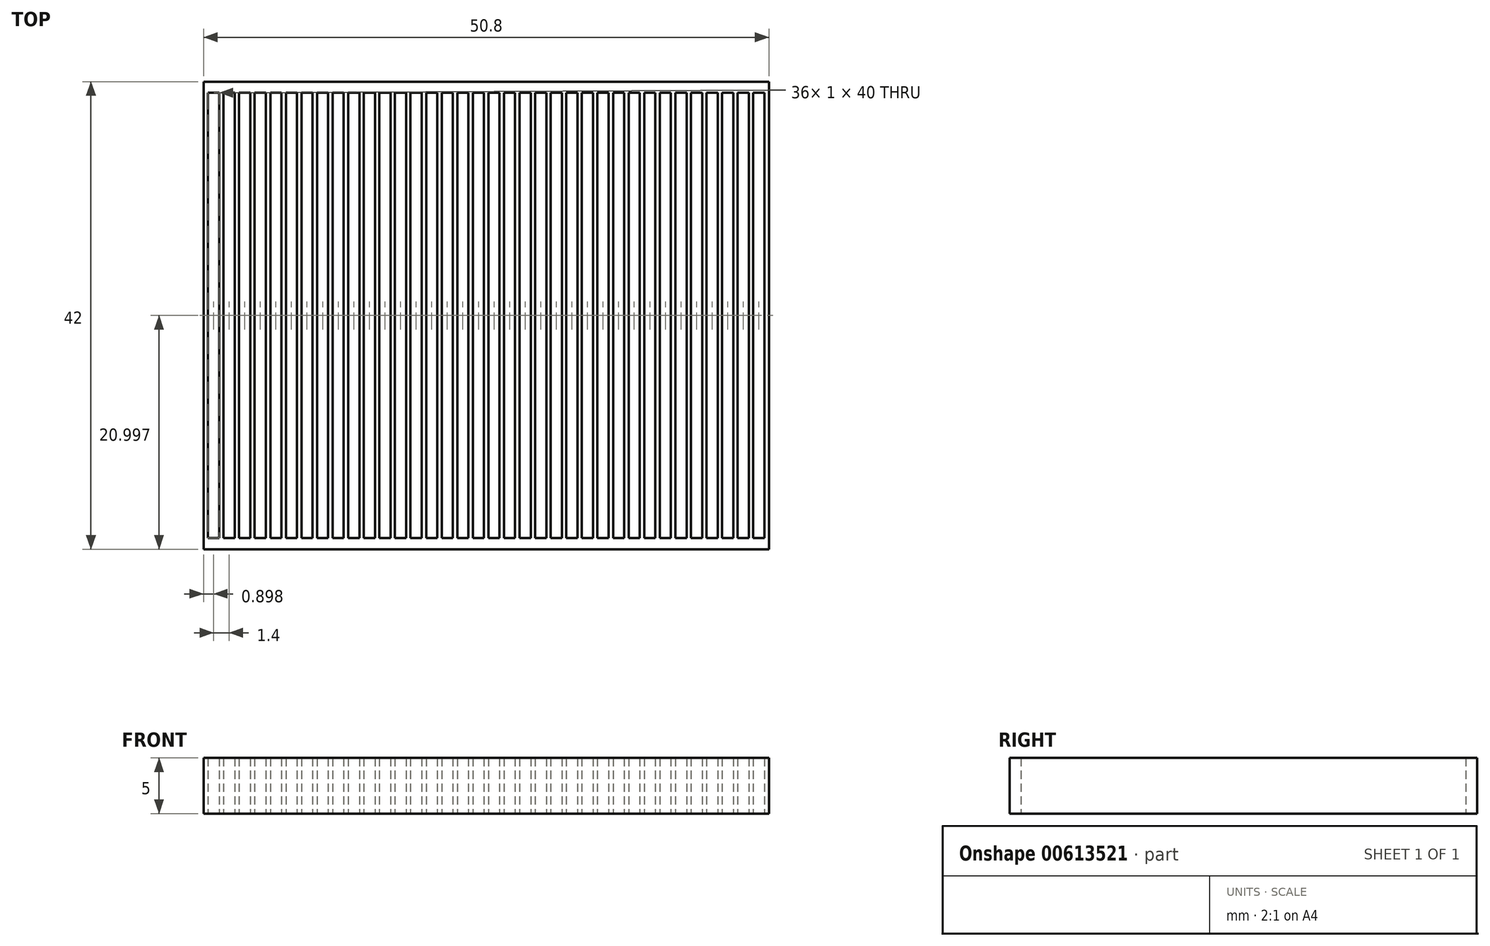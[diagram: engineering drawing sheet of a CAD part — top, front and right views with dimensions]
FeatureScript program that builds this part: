
annotation { "Feature Type Name" : "Feature", "Feature Type Description" : "" }
export const myFeature = defineFeature(function(context is Context, id is Id, definition is map)
    precondition{}
    {
        {
            var Q0;
            Q0=qCreatedBy(makeId("Top.planeOp"),FACE);
            var sketch = newSketch(context, id + "F0", { "sketchPlane" : qUnion([Q0])});
            skLineSegment(sketch, "E0", {"start": v(-21.82, 27.89) * mm, "end": v(-21.82, -14.11) * mm});
            skLineSegment(sketch, "E1", {"start": v(-21.82, -14.11) * mm, "end": v(-21.42, -14.11) * mm});
            skLineSegment(sketch, "E2", {"start": v(-21.42, -14.11) * mm, "end": v(-21.42, 26.89) * mm});
            skLineSegment(sketch, "E3", {"start": v(-21.42, 26.89) * mm, "end": v(-20.42, 26.89) * mm});
            skLineSegment(sketch, "E4", {"start": v(-20.42, 26.89) * mm, "end": v(-20.42, -14.11) * mm});
            skLineSegment(sketch, "E5", {"start": v(-20.42, -14.11) * mm, "end": v(-20.02, -14.11) * mm});
            skLineSegment(sketch, "E6", {"start": v(-20.02, -14.11) * mm, "end": v(-20.02, 26.89) * mm});
            skLineSegment(sketch, "E7", {"start": v(-20.02, 26.89) * mm, "end": v(-19.02, 26.89) * mm});
            skLineSegment(sketch, "E8", {"start": v(-19.02, 26.89) * mm, "end": v(-19.02, -14.11) * mm});
            skLineSegment(sketch, "E9", {"start": v(-19.02, -14.11) * mm, "end": v(-18.62, -14.11) * mm});
            skLineSegment(sketch, "E10", {"start": v(-18.62, -14.11) * mm, "end": v(-18.62, 26.89) * mm});
            skLineSegment(sketch, "E11", {"start": v(-18.62, 26.89) * mm, "end": v(-17.62, 26.89) * mm});
            skLineSegment(sketch, "E12", {"start": v(-17.62, 26.89) * mm, "end": v(-17.62, -14.11) * mm});
            skLineSegment(sketch, "E13", {"start": v(-17.62, -14.11) * mm, "end": v(-17.22, -14.11) * mm});
            skLineSegment(sketch, "E14", {"start": v(-17.22, -14.11) * mm, "end": v(-17.22, 26.89) * mm});
            skLineSegment(sketch, "E15", {"start": v(-17.22, 26.89) * mm, "end": v(-16.22, 26.89) * mm});
            skLineSegment(sketch, "E16", {"start": v(-16.22, 26.89) * mm, "end": v(-16.22, -14.11) * mm});
            skLineSegment(sketch, "E17", {"start": v(-16.22, -14.11) * mm, "end": v(-15.82, -14.11) * mm});
            skLineSegment(sketch, "E18", {"start": v(-15.82, -14.11) * mm, "end": v(-15.82, 26.89) * mm});
            skLineSegment(sketch, "E19", {"start": v(-15.82, 26.89) * mm, "end": v(-14.82, 26.89) * mm});
            skLineSegment(sketch, "E20", {"start": v(-14.82, 26.89) * mm, "end": v(-14.82, -14.11) * mm});
            skLineSegment(sketch, "E21", {"start": v(-14.82, -14.11) * mm, "end": v(-14.42, -14.11) * mm});
            skLineSegment(sketch, "E22", {"start": v(-14.42, -14.11) * mm, "end": v(-14.42, 26.89) * mm});
            skLineSegment(sketch, "E23", {"start": v(-14.42, 26.89) * mm, "end": v(-13.42, 26.89) * mm});
            skLineSegment(sketch, "E24", {"start": v(-13.42, 26.89) * mm, "end": v(-13.42, -14.11) * mm});
            skLineSegment(sketch, "E25", {"start": v(-13.42, -14.11) * mm, "end": v(-13.02, -14.11) * mm});
            skLineSegment(sketch, "E26", {"start": v(-13.02, -14.11) * mm, "end": v(-13.02, 26.89) * mm});
            skLineSegment(sketch, "E27", {"start": v(-13.02, 26.89) * mm, "end": v(-12.02, 26.89) * mm});
            skLineSegment(sketch, "E28", {"start": v(-12.02, 26.89) * mm, "end": v(-12.02, -14.11) * mm});
            skLineSegment(sketch, "E29", {"start": v(-12.02, -14.11) * mm, "end": v(-11.62, -14.11) * mm});
            skLineSegment(sketch, "E30", {"start": v(-11.62, -14.11) * mm, "end": v(-11.62, 26.89) * mm});
            skLineSegment(sketch, "E31", {"start": v(-11.62, 26.89) * mm, "end": v(-10.62, 26.89) * mm});
            skLineSegment(sketch, "E32", {"start": v(-10.62, 26.89) * mm, "end": v(-10.62, -14.11) * mm});
            skLineSegment(sketch, "E33", {"start": v(-10.62, -14.11) * mm, "end": v(-10.22, -14.11) * mm});
            skLineSegment(sketch, "E34", {"start": v(-10.22, -14.11) * mm, "end": v(-10.22, 26.89) * mm});
            skLineSegment(sketch, "E35", {"start": v(-10.22, 26.89) * mm, "end": v(-9.22, 26.89) * mm});
            skLineSegment(sketch, "E36", {"start": v(-9.22, 26.89) * mm, "end": v(-9.22, -14.11) * mm});
            skLineSegment(sketch, "E37", {"start": v(-9.22, -14.11) * mm, "end": v(-8.82, -14.11) * mm});
            skLineSegment(sketch, "E38", {"start": v(-8.82, -14.11) * mm, "end": v(-8.82, 26.89) * mm});
            skLineSegment(sketch, "E39", {"start": v(-8.82, 26.89) * mm, "end": v(-7.82, 26.89) * mm});
            skLineSegment(sketch, "E40", {"start": v(-7.82, 26.89) * mm, "end": v(-7.82, -14.11) * mm});
            skLineSegment(sketch, "E41", {"start": v(-7.82, -14.11) * mm, "end": v(-7.42, -14.11) * mm});
            skLineSegment(sketch, "E42", {"start": v(-7.42, -14.11) * mm, "end": v(-7.42, 26.89) * mm});
            skLineSegment(sketch, "E43", {"start": v(-7.42, 26.89) * mm, "end": v(-6.42, 26.89) * mm});
            skLineSegment(sketch, "E44", {"start": v(-6.42, 26.89) * mm, "end": v(-6.42, -14.11) * mm});
            skLineSegment(sketch, "E45", {"start": v(-6.42, -14.11) * mm, "end": v(-6.02, -14.11) * mm});
            skLineSegment(sketch, "E46", {"start": v(-6.02, -14.11) * mm, "end": v(-6.02, 26.89) * mm});
            skLineSegment(sketch, "E47", {"start": v(-6.02, 26.89) * mm, "end": v(-5.02, 26.89) * mm});
            skLineSegment(sketch, "E48", {"start": v(-5.02, 26.89) * mm, "end": v(-5.02, -14.11) * mm});
            skLineSegment(sketch, "E49", {"start": v(-5.02, -14.11) * mm, "end": v(-4.62, -14.11) * mm});
            skLineSegment(sketch, "E50", {"start": v(-4.62, -14.11) * mm, "end": v(-4.62, 26.89) * mm});
            skLineSegment(sketch, "E51", {"start": v(-4.62, 26.89) * mm, "end": v(-3.62, 26.89) * mm});
            skLineSegment(sketch, "E52", {"start": v(-3.62, 26.89) * mm, "end": v(-3.62, -14.11) * mm});
            skLineSegment(sketch, "E53", {"start": v(-3.62, -14.11) * mm, "end": v(-3.22, -14.11) * mm});
            skLineSegment(sketch, "E54", {"start": v(-3.22, -14.11) * mm, "end": v(-3.22, 26.89) * mm});
            skLineSegment(sketch, "E55", {"start": v(-3.22, 26.89) * mm, "end": v(-2.22, 26.89) * mm});
            skLineSegment(sketch, "E56", {"start": v(-2.22, 26.89) * mm, "end": v(-2.22, -14.11) * mm});
            skLineSegment(sketch, "E57", {"start": v(-2.22, -14.11) * mm, "end": v(-1.82, -14.11) * mm});
            skLineSegment(sketch, "E58", {"start": v(-1.82, -14.11) * mm, "end": v(-1.82, 26.89) * mm});
            skLineSegment(sketch, "E59", {"start": v(-1.82, 26.89) * mm, "end": v(-0.82, 26.89) * mm});
            skLineSegment(sketch, "E60", {"start": v(-0.82, 26.89) * mm, "end": v(-0.82, -14.11) * mm});
            skLineSegment(sketch, "E61", {"start": v(-0.82, -14.11) * mm, "end": v(-0.42, -14.11) * mm});
            skLineSegment(sketch, "E62", {"start": v(-0.42, -14.11) * mm, "end": v(-0.42, 26.89) * mm});
            skLineSegment(sketch, "E63", {"start": v(-0.42, 26.89) * mm, "end": v(0.58, 26.89) * mm});
            skLineSegment(sketch, "E64", {"start": v(0.58, 26.89) * mm, "end": v(0.58, -14.11) * mm});
            skLineSegment(sketch, "E65", {"start": v(0.58, -14.11) * mm, "end": v(0.98, -14.11) * mm});
            skLineSegment(sketch, "E66", {"start": v(0.98, -14.11) * mm, "end": v(0.98, 26.89) * mm});
            skLineSegment(sketch, "E67", {"start": v(0.98, 26.89) * mm, "end": v(1.98, 26.89) * mm});
            skLineSegment(sketch, "E68", {"start": v(1.98, 26.89) * mm, "end": v(1.98, -14.11) * mm});
            skLineSegment(sketch, "E69", {"start": v(1.98, -14.11) * mm, "end": v(2.38, -14.11) * mm});
            skLineSegment(sketch, "E70", {"start": v(2.38, -14.11) * mm, "end": v(2.38, 26.89) * mm});
            skLineSegment(sketch, "E71", {"start": v(2.38, 26.89) * mm, "end": v(3.38, 26.89) * mm});
            skLineSegment(sketch, "E72", {"start": v(3.38, 26.89) * mm, "end": v(3.38, -14.11) * mm});
            skLineSegment(sketch, "E73", {"start": v(3.38, -14.11) * mm, "end": v(3.78, -14.11) * mm});
            skLineSegment(sketch, "E74", {"start": v(3.78, -14.11) * mm, "end": v(3.78, 26.89) * mm});
            skLineSegment(sketch, "E75", {"start": v(3.78, 26.89) * mm, "end": v(4.78, 26.89) * mm});
            skLineSegment(sketch, "E76", {"start": v(4.78, 26.89) * mm, "end": v(4.78, -14.11) * mm});
            skLineSegment(sketch, "E77", {"start": v(4.78, -14.11) * mm, "end": v(5.18, -14.11) * mm});
            skLineSegment(sketch, "E78", {"start": v(5.18, -14.11) * mm, "end": v(5.18, 26.89) * mm});
            skLineSegment(sketch, "E79", {"start": v(5.18, 26.89) * mm, "end": v(6.18, 26.89) * mm});
            skLineSegment(sketch, "E80", {"start": v(6.18, 26.89) * mm, "end": v(6.18, -14.11) * mm});
            skLineSegment(sketch, "E81", {"start": v(6.18, -14.11) * mm, "end": v(6.58, -14.11) * mm});
            skLineSegment(sketch, "E82", {"start": v(6.58, -14.11) * mm, "end": v(6.58, 26.89) * mm});
            skLineSegment(sketch, "E83", {"start": v(6.58, 26.89) * mm, "end": v(7.58, 26.89) * mm});
            skLineSegment(sketch, "E84", {"start": v(7.58, 26.89) * mm, "end": v(7.58, -14.11) * mm});
            skLineSegment(sketch, "E85", {"start": v(7.58, -14.11) * mm, "end": v(7.98, -14.11) * mm});
            skLineSegment(sketch, "E86", {"start": v(7.98, -14.11) * mm, "end": v(7.98, 26.89) * mm});
            skLineSegment(sketch, "E87", {"start": v(7.98, 26.89) * mm, "end": v(8.98, 26.89) * mm});
            skLineSegment(sketch, "E88", {"start": v(8.98, 26.89) * mm, "end": v(8.98, -14.11) * mm});
            skLineSegment(sketch, "E89", {"start": v(8.98, -14.11) * mm, "end": v(9.38, -14.11) * mm});
            skLineSegment(sketch, "E90", {"start": v(9.38, -14.11) * mm, "end": v(9.38, 26.89) * mm});
            skLineSegment(sketch, "E91", {"start": v(9.38, 26.89) * mm, "end": v(10.38, 26.89) * mm});
            skLineSegment(sketch, "E92", {"start": v(10.38, 26.89) * mm, "end": v(10.38, -14.11) * mm});
            skLineSegment(sketch, "E93", {"start": v(10.38, -14.11) * mm, "end": v(10.78, -14.11) * mm});
            skLineSegment(sketch, "E94", {"start": v(10.78, -14.11) * mm, "end": v(10.78, 26.89) * mm});
            skLineSegment(sketch, "E95", {"start": v(10.78, 26.89) * mm, "end": v(11.78, 26.89) * mm});
            skLineSegment(sketch, "E96", {"start": v(11.78, 26.89) * mm, "end": v(11.78, -14.11) * mm});
            skLineSegment(sketch, "E97", {"start": v(11.78, -14.11) * mm, "end": v(12.18, -14.11) * mm});
            skLineSegment(sketch, "E98", {"start": v(12.18, -14.11) * mm, "end": v(12.18, 26.89) * mm});
            skLineSegment(sketch, "E99", {"start": v(12.18, 26.89) * mm, "end": v(13.18, 26.89) * mm});
            skLineSegment(sketch, "E100", {"start": v(13.18, 26.89) * mm, "end": v(13.18, -14.11) * mm});
            skLineSegment(sketch, "E101", {"start": v(13.18, -14.11) * mm, "end": v(13.58, -14.11) * mm});
            skLineSegment(sketch, "E102", {"start": v(13.58, -14.11) * mm, "end": v(13.58, 26.89) * mm});
            skLineSegment(sketch, "E103", {"start": v(13.58, 26.89) * mm, "end": v(14.58, 26.89) * mm});
            skLineSegment(sketch, "E104", {"start": v(14.58, 26.89) * mm, "end": v(14.58, -14.11) * mm});
            skLineSegment(sketch, "E105", {"start": v(14.58, -14.11) * mm, "end": v(14.98, -14.11) * mm});
            skLineSegment(sketch, "E106", {"start": v(14.98, -14.11) * mm, "end": v(14.98, 26.89) * mm});
            skLineSegment(sketch, "E107", {"start": v(14.98, 26.89) * mm, "end": v(15.98, 26.89) * mm});
            skLineSegment(sketch, "E108", {"start": v(15.98, 26.89) * mm, "end": v(15.98, -14.11) * mm});
            skLineSegment(sketch, "E109", {"start": v(15.98, -14.11) * mm, "end": v(16.38, -14.11) * mm});
            skLineSegment(sketch, "E110", {"start": v(16.38, -14.11) * mm, "end": v(16.38, 26.89) * mm});
            skLineSegment(sketch, "E111", {"start": v(16.38, 26.89) * mm, "end": v(17.38, 26.89) * mm});
            skLineSegment(sketch, "E112", {"start": v(17.38, 26.89) * mm, "end": v(17.38, -14.11) * mm});
            skLineSegment(sketch, "E113", {"start": v(17.38, -14.11) * mm, "end": v(17.78, -14.11) * mm});
            skLineSegment(sketch, "E114", {"start": v(17.78, -14.11) * mm, "end": v(17.78, 26.89) * mm});
            skLineSegment(sketch, "E115", {"start": v(17.78, 26.89) * mm, "end": v(18.78, 26.89) * mm});
            skLineSegment(sketch, "E116", {"start": v(18.78, 26.89) * mm, "end": v(18.78, -14.11) * mm});
            skLineSegment(sketch, "E117", {"start": v(18.78, -14.11) * mm, "end": v(19.18, -14.11) * mm});
            skLineSegment(sketch, "E118", {"start": v(19.18, -14.11) * mm, "end": v(19.18, 26.89) * mm});
            skLineSegment(sketch, "E119", {"start": v(19.18, 26.89) * mm, "end": v(20.18, 26.89) * mm});
            skLineSegment(sketch, "E120", {"start": v(20.18, 26.89) * mm, "end": v(20.18, -14.11) * mm});
            skLineSegment(sketch, "E121", {"start": v(20.18, -14.11) * mm, "end": v(20.58, -14.11) * mm});
            skLineSegment(sketch, "E122", {"start": v(20.58, -14.11) * mm, "end": v(20.58, 26.89) * mm});
            skLineSegment(sketch, "E123", {"start": v(20.58, 26.89) * mm, "end": v(21.58, 26.89) * mm});
            skLineSegment(sketch, "E124", {"start": v(21.58, 26.89) * mm, "end": v(21.58, -14.11) * mm});
            skLineSegment(sketch, "E125", {"start": v(21.58, -14.11) * mm, "end": v(21.98, -14.11) * mm});
            skLineSegment(sketch, "E126", {"start": v(21.98, -14.11) * mm, "end": v(21.98, 26.89) * mm});
            skLineSegment(sketch, "E127", {"start": v(21.98, 26.89) * mm, "end": v(22.98, 26.89) * mm});
            skLineSegment(sketch, "E128", {"start": v(22.98, 26.89) * mm, "end": v(22.98, -14.11) * mm});
            skLineSegment(sketch, "E129", {"start": v(22.98, -14.11) * mm, "end": v(23.38, -14.11) * mm});
            skLineSegment(sketch, "E130", {"start": v(23.38, -14.11) * mm, "end": v(23.38, 26.89) * mm});
            skLineSegment(sketch, "E131", {"start": v(23.38, 26.89) * mm, "end": v(24.38, 26.89) * mm});
            skLineSegment(sketch, "E132", {"start": v(24.38, 26.89) * mm, "end": v(24.38, -14.11) * mm});
            skLineSegment(sketch, "E133", {"start": v(24.38, -14.11) * mm, "end": v(24.78, -14.11) * mm});
            skLineSegment(sketch, "E134", {"start": v(24.78, -14.11) * mm, "end": v(24.78, 26.89) * mm});
            skLineSegment(sketch, "E135", {"start": v(24.78, 26.89) * mm, "end": v(25.78, 26.89) * mm});
            skLineSegment(sketch, "E136", {"start": v(25.78, 26.89) * mm, "end": v(25.78, -14.11) * mm});
            skLineSegment(sketch, "E137", {"start": v(25.78, -14.11) * mm, "end": v(26.18, -14.11) * mm});
            skLineSegment(sketch, "E138", {"start": v(26.18, -14.11) * mm, "end": v(26.18, 26.89) * mm});
            skLineSegment(sketch, "E139", {"start": v(26.18, 26.89) * mm, "end": v(27.18, 26.89) * mm});
            skLineSegment(sketch, "E140", {"start": v(27.18, 26.89) * mm, "end": v(27.18, -14.11) * mm});
            skLineSegment(sketch, "E141", {"start": v(27.18, -14.11) * mm, "end": v(27.58, -14.11) * mm});
            skLineSegment(sketch, "E142", {"start": v(27.58, -14.11) * mm, "end": v(27.58, 26.89) * mm});
            skLineSegment(sketch, "E143", {"start": v(27.58, 26.89) * mm, "end": v(28.58, 26.89) * mm});
            skLineSegment(sketch, "E144", {"start": v(28.58, 26.89) * mm, "end": v(28.58, -14.11) * mm});
            skLineSegment(sketch, "E145", {"start": v(28.58, -14.11) * mm, "end": v(28.98, -14.11) * mm});
            skLineSegment(sketch, "E146", {"start": v(28.98, -14.11) * mm, "end": v(28.98, 26.89) * mm});
            skLineSegment(sketch, "E147", {"start": v(28.98, 26.89) * mm, "end": v(28.98, 27.89) * mm});
            skLineSegment(sketch, "E148", {"start": v(28.98, 27.89) * mm, "end": v(-21.82, 27.89) * mm});
            skLineSegment(sketch, "E149.bottom", {"start": v(-21.82, -14.11) * mm, "end": v(28.58, -14.11) * mm});
            skLineSegment(sketch, "E149.top", {"start": v(-21.82, -13.11) * mm, "end": v(28.58, -13.11) * mm});
            skLineSegment(sketch, "E149.left", {"start": v(-21.82, -14.11) * mm, "end": v(-21.82, -13.11) * mm});
            skLineSegment(sketch, "E149.right", {"start": v(28.58, -14.11) * mm, "end": v(28.58, -13.11) * mm});
            skSolve(sketch);
        }
        {
            var Q0;
            Q0 = qSketchRegion(id + "F0", true);
            extrude(context, id + "F1", {"entities" : qUnion([Q0]), "depth" : 5 * mm, "offsetDistance" : 25 * mm});
        }
    });
